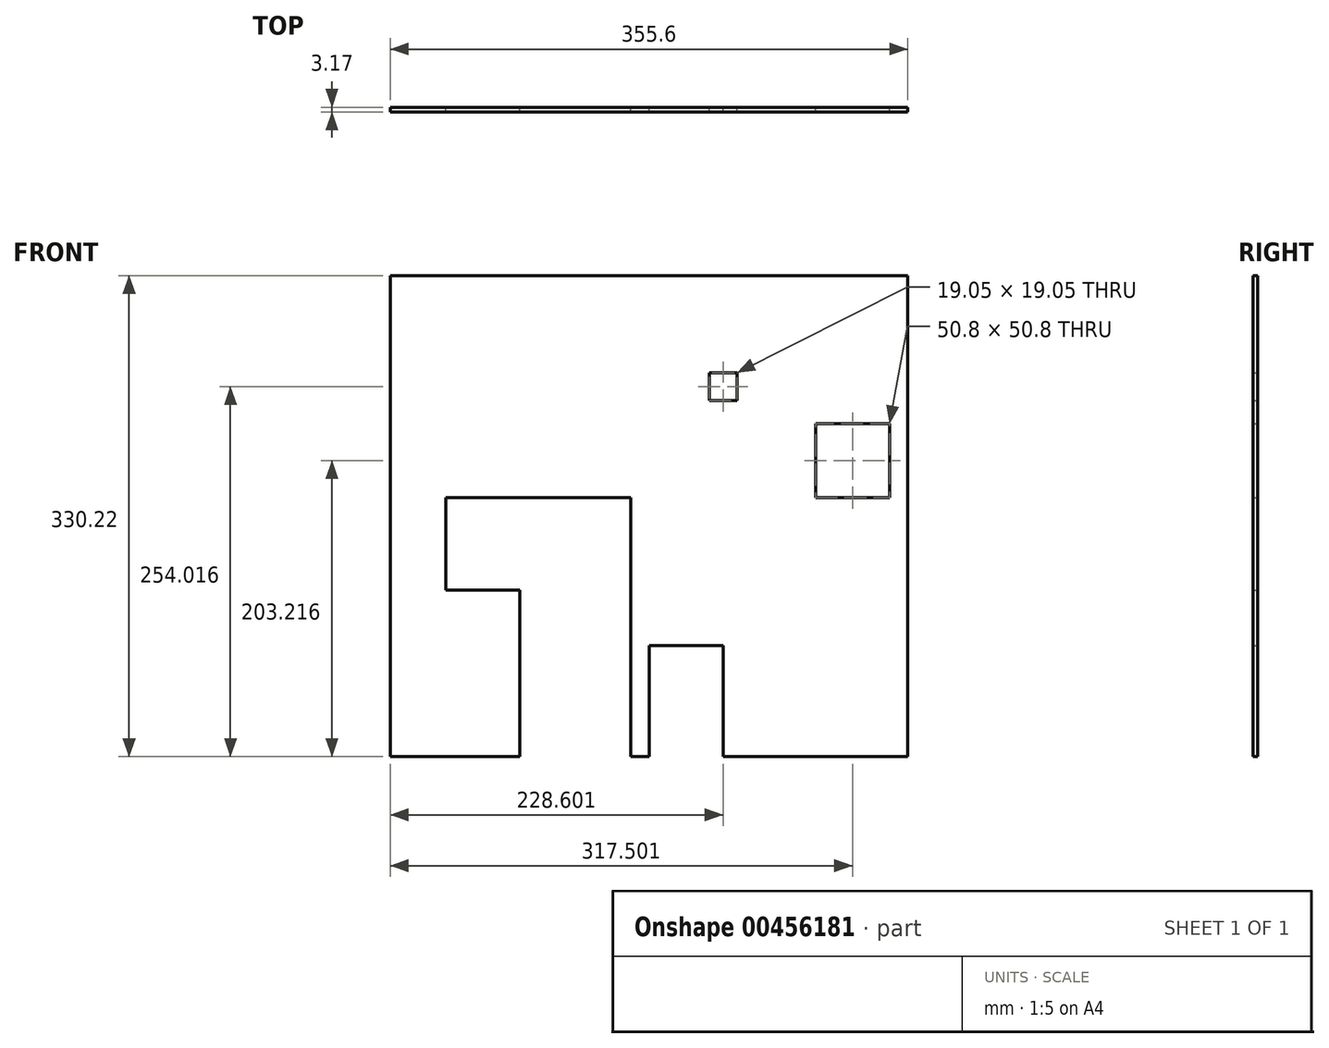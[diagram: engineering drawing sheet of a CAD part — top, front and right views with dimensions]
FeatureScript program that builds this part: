
annotation { "Feature Type Name" : "Feature", "Feature Type Description" : "" }
export const myFeature = defineFeature(function(context is Context, id is Id, definition is map)
    precondition{}
    {
        {
            var Q0;
            Q0=qCreatedBy(makeId("Front.planeOp"),FACE);
            var sketch = newSketch(context, id + "F0", { "sketchPlane" : qUnion([Q0])});
            skLineSegment(sketch, "E0.bottom", {"start": v(-170.18, 200.02) * mm, "end": v(185.42, 200.02) * mm});
            skLineSegment(sketch, "E0.top", {"start": v(-170.18, -130.18) * mm, "end": v(-132.08, -130.18) * mm});
            skLineSegment(sketch, "E0.left", {"start": v(-170.18, 200.02) * mm, "end": v(-170.18, -130.18) * mm});
            skLineSegment(sketch, "E0.right", {"start": v(185.42, 200.02) * mm, "end": v(185.42, -130.18) * mm});
            skLineSegment(sketch, "E1", {"start": v(-5.08, 47.62) * mm, "end": v(-5.08, -130.18) * mm});
            skLineSegment(sketch, "E2", {"start": v(-132.08, -15.88) * mm, "end": v(-132.08, 47.62) * mm});
            skLineSegment(sketch, "E3", {"start": v(58.42, -130.18) * mm, "end": v(58.42, -53.98) * mm});
            skLineSegment(sketch, "E4", {"start": v(7.62, -130.18) * mm, "end": v(7.62, -53.98) * mm});
            skLineSegment(sketch, "E5", {"start": v(7.62, -53.98) * mm, "end": v(58.42, -53.98) * mm});
            skPoint(sketch, "E6.orphan", {"position": v(7.62, 200.02) * mm});
            skLineSegment(sketch, "E7.trimOffspring", {"start": v(58.42, -130.18) * mm, "end": v(185.42, -130.18) * mm});
            skLineSegment(sketch, "E8.trimOffspring", {"start": v(-5.08, -130.18) * mm, "end": v(7.62, -130.18) * mm});
            skLineSegment(sketch, "E9", {"start": v(-132.08, -15.88) * mm, "end": v(-81.28, -15.88) * mm});
            skLineSegment(sketch, "E10", {"start": v(-81.28, -15.88) * mm, "end": v(-81.28, -130.2) * mm});
            skLineSegment(sketch, "E11", {"start": v(-81.28, -130.2) * mm, "end": v(-132.08, -130.18) * mm});
            skLineSegment(sketch, "E12", {"start": v(-132.08, 47.62) * mm, "end": v(-5.08, 47.62) * mm});
            skPoint(sketch, "E13.end.orphan", {"position": v(-81.28, 47.62) * mm});
            skLineSegment(sketch, "E14.bottom", {"start": v(121.92, 98.42) * mm, "end": v(172.72, 98.42) * mm});
            skLineSegment(sketch, "E14.top", {"start": v(121.92, 47.62) * mm, "end": v(172.72, 47.62) * mm});
            skLineSegment(sketch, "E14.left", {"start": v(121.92, 98.42) * mm, "end": v(121.92, 47.62) * mm});
            skLineSegment(sketch, "E14.right", {"start": v(172.72, 98.42) * mm, "end": v(172.72, 47.62) * mm});
            skPoint(sketch, "E15", {"position": v(147.32, 73.02) * mm});
            skPoint(sketch, "E15.positionSnap0", {"position": v(121.92, 73.02) * mm});
            skPoint(sketch, "E15.positionSnap1", {"position": v(147.32, 98.42) * mm});
            skLineSegment(sketch, "E16.bottom", {"start": v(48.9, 133.34) * mm, "end": v(67.95, 133.34) * mm});
            skLineSegment(sketch, "E16.top", {"start": v(48.9, 114.3) * mm, "end": v(67.95, 114.3) * mm});
            skLineSegment(sketch, "E16.left", {"start": v(48.9, 133.34) * mm, "end": v(48.9, 114.3) * mm});
            skLineSegment(sketch, "E16.right", {"start": v(67.95, 133.34) * mm, "end": v(67.95, 114.3) * mm});
            skLineSegment(sketch, "E17", {"start": v(185.42, 114.3) * mm, "end": v(67.95, 114.3) * mm});
            skSolve(sketch);
        }
        {
            var Q0;
            Q0=makeQuery(id+"F0.imprint","IMPRINT",FACE,{"disambiguationData":[TD([[makeQuery(id+"F0.imprint","IMPRINT",EDGE,{"derivedFrom":sQuery(id+"F0.wireOp",EDGE,"E0.bottom")}),-1.0]])]});
            extrude(context, id + "F1", {"entities" : qUnion([Q0]), "depth" : 3.17 * mm});
        }
    });
